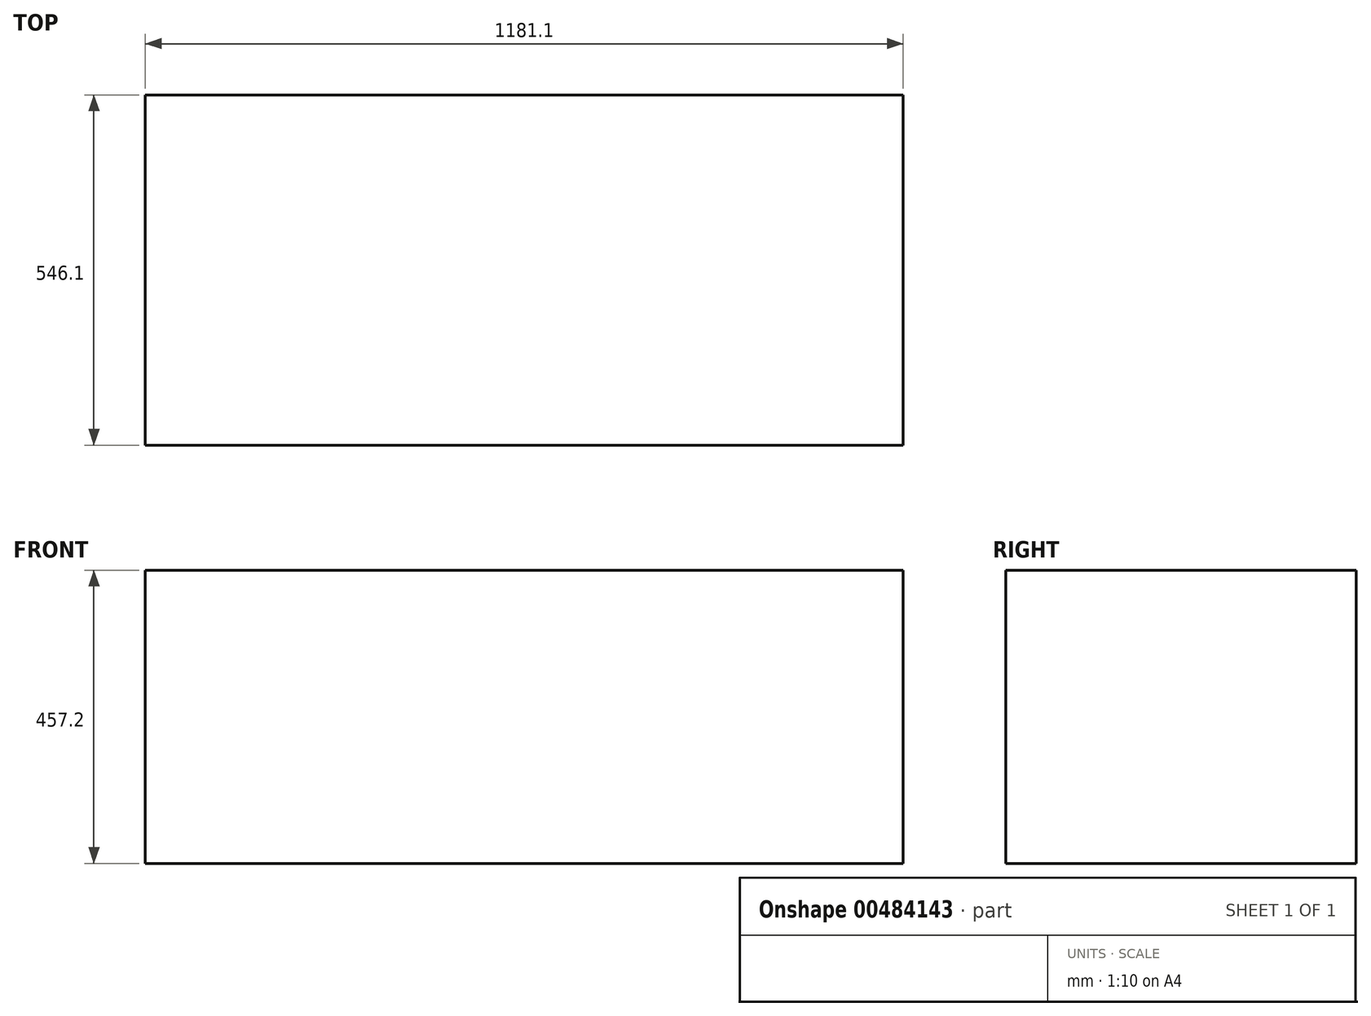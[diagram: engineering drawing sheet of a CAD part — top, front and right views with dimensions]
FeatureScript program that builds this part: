
annotation { "Feature Type Name" : "Feature", "Feature Type Description" : "" }
export const myFeature = defineFeature(function(context is Context, id is Id, definition is map)
    precondition{}
    {
        {
            var Q0;
            Q0=qCreatedBy(makeId("Front.planeOp"),FACE);
            var sketch = newSketch(context, id + "F0", { "sketchPlane" : qUnion([Q0])});
            skLineSegment(sketch, "E0.bottom", {"start": v(0, 0) * mm, "end": v(1181.1, 0) * mm});
            skLineSegment(sketch, "E0.top", {"start": v(0, 457.2) * mm, "end": v(1181.1, 457.2) * mm});
            skLineSegment(sketch, "E0.left", {"start": v(0, 0) * mm, "end": v(0, 457.2) * mm});
            skLineSegment(sketch, "E0.right", {"start": v(1181.1, 0) * mm, "end": v(1181.1, 457.2) * mm});
            skSolve(sketch);
        }
        {
            var Q0;
            Q0 = qSketchRegion(id + "F0", true);
            extrude(context, id + "F1", {"entities" : qUnion([Q0]), "depth" : 546.1 * mm, "offsetDistance" : 25.4 * mm});
        }
    });
